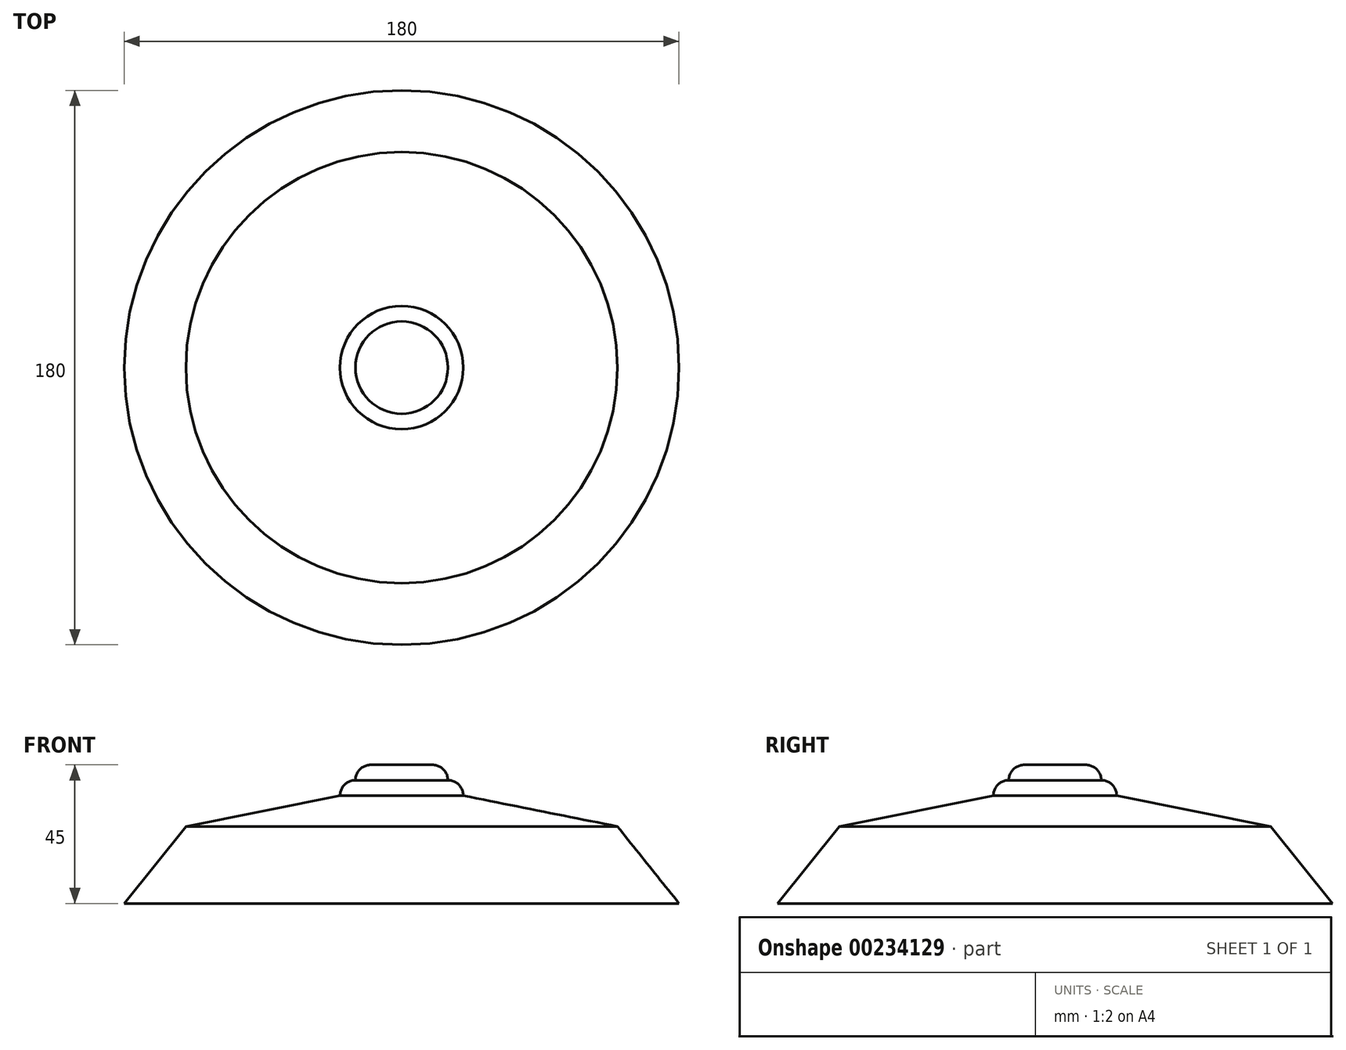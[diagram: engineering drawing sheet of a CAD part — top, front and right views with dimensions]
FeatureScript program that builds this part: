
annotation { "Feature Type Name" : "Feature", "Feature Type Description" : "" }
export const myFeature = defineFeature(function(context is Context, id is Id, definition is map)
    precondition{}
    {
        {
            var Q0;
            Q0=qCreatedBy(makeId("Front.planeOp"),FACE);
            var sketch = newSketch(context, id + "F0", { "sketchPlane" : qUnion([Q0])});
            skLineSegment(sketch, "E0", {"start": v(-90, 0) * mm, "end": v(-70, 25) * mm});
            skLineSegment(sketch, "E1", {"start": v(-70, 25) * mm, "end": v(-20, 35) * mm});
            skLineSegment(sketch, "E2", {"start": v(-20, 35) * mm, "end": v(-20, 40) * mm});
            skLineSegment(sketch, "E3", {"start": v(-20, 40) * mm, "end": v(-15, 40) * mm});
            skLineSegment(sketch, "E4", {"start": v(-15, 40) * mm, "end": v(-15, 45) * mm});
            skLineSegment(sketch, "E5", {"start": v(-15, 45) * mm, "end": v(0, 45) * mm});
            skLineSegment(sketch, "E6", {"start": v(0, 45) * mm, "end": v(0, 0) * mm});
            skLineSegment(sketch, "E7", {"start": v(0, 0) * mm, "end": v(-90, 0) * mm});
            skSolve(sketch);
        }
        {
            var Q0;
            Q0=makeQuery(id+"F0.imprint","IMPRINT",FACE,{"disambiguationData":[TD([[makeQuery(id+"F0.imprint","IMPRINT",EDGE,{"derivedFrom":sQuery(id+"F0.wireOp",EDGE,"E0")}),-1.0]])]});
            var Q1;
            Q1=sQuery(id+"F0.wireOp",EDGE,"E6");
            revolve(context, id + "F1", {"entities" : qUnion([Q0]), "axis" : qUnion([Q1]), "revolveType" : RevolveType.FULL});
        }
        {
            var Q0;
            Q0=makeQuery(id+"F1.opRevolve","SWEPT_EDGE",EDGE,{"disambiguationData":[OSD([sQuery(id+"F0.wireOp",EDGE,"E2"),sQuery(id+"F0.wireOp",EDGE,"E3")])]});
            var Q1;
            Q1=makeQuery(id+"F1.opRevolve","SWEPT_EDGE",EDGE,{"disambiguationData":[OSD([sQuery(id+"F0.wireOp",EDGE,"E4"),sQuery(id+"F0.wireOp",EDGE,"E5")])]});
            fillet(context, id + "F2", {"entities" : qUnion([Q0, Q1]), "radius" : 5 * mm, "tangentPropagation" : true, "allowEdgeOverflow" : false});
        }
    });
